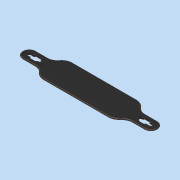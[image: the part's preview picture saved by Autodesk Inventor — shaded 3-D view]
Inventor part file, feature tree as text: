
AUTODESK INVENTOR PART (.ipt)
format: ipt  version: 2017 (Build 210142000, 142)  size: 602,112 bytes
history: native  units: mm
features: extrude x5, sketch x5, fillet x2
ambient origin geometry x8: Origin, YZ Plane, XZ Plane, XY Plane, X Axis, Y Axis, Z Axis, Center Point
bodies: Volumenkörper1 (feature_tree)
feature tree (12):
  extrude  "Extrusion1"  Depth=70.0mm TaperAngle=0.0deg
  extrude  "Extrusion2"  Depth=25.0mm
  extrude  "Extrusion3"  Depth=12.0mm
  extrude  "Extrusion4"  Depth=2000.0mm TaperAngle=0.0deg
  extrude  "Extrusion5"  Depth=5.0mm
  fillet  "Rundung1"  Radius=220.0mm
  fillet  "Rundung2"  Radius=2000.0mm
  sketch  "Skizze1"  dims[d0=70.0mm d1=0.0mm d2=70.0mm d3=0.0mm]
  sketch  "Skizze2"  dims[d4=25.0mm d5=25.0mm]
  sketch  "Skizze3"  dims[d6=220.0mm d7=12.0mm]
  sketch  "Skizze5"  dims[d8=25.0mm d9=2000.0mm d10=0.0mm]
  sketch  "Skizze6"  dims[d11=12.0mm d12=13.0mm d13=220.0mm d14=2000.0mm d15=0.0mm d16=199.5mm d17=0.0mm d18=5.0mm d19=5.0mm]
